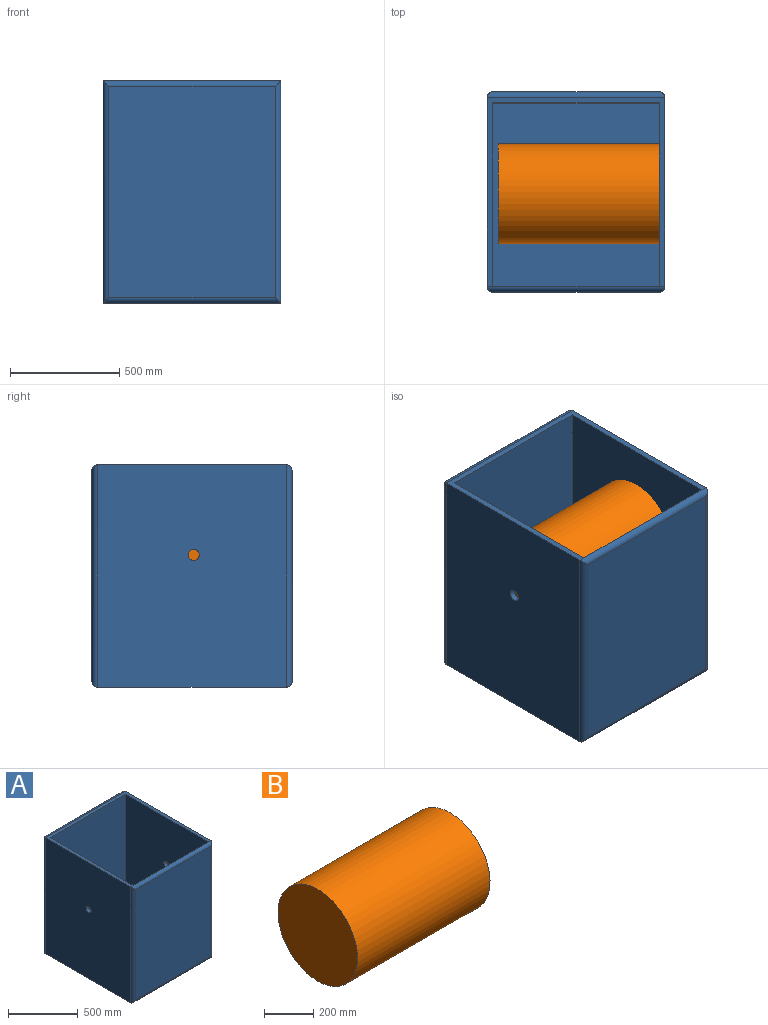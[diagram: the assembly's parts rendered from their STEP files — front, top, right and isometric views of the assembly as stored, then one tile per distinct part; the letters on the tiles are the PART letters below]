
ASSEMBLY  parts=2 mates=1
PART A: 21 faces, bbox 812.8x914.4x1016 mm
  f0: plane 863.6x812.8mm, normal (0,0,1), area 63225.7mm2, adj f2,f4,f6,f7,f9,f12,f16
  f1: plane 965.2x762mm, normal (0,1,0), area 735482.4mm2, adj f11,f12,f13,f14
  f2: plane 1016x863.6mm, normal (-1,0,0), area 875390.8mm2, adj f0,f5,f14,f18,f20
  f3: plane 965.2x762mm, normal (0,-1,0), area 735482.4mm2, adj f15,f16,f17,f18
  f4: plane 1016x863.6mm, normal (1,0,0), area 875390.8mm2, adj f0,f5,f11,f15,f19
  f5: plane 863.6x812.8mm, normal (0,0,-1), area 701934.1mm2, adj f2,f4,f13,f17
  f6: plane 939.8x762mm, normal (0,-1,0), area 716127.6mm2, adj f0,f7,f9,f10
  f7: plane 939.8x838.2mm, normal (1,0,0), area 785713.5mm2, adj f0,f6,f8,f10,f20
  f8: plane 939.8x762mm, normal (0,1,0), area 716127.6mm2, adj f7,f9,f10,f16
  f9: plane 939.8x838.2mm, normal (-1,0,0), area 785713.5mm2, adj f0,f6,f8,f10,f19
  f10: plane 838.2x762mm, normal (0,0,1), area 638708.4mm2, adj f6,f7,f8,f9
  f11: cylinder r=25.4mm len=1016mm, axis (0,0,-1), area 39800.1mm2, adj f1,f4,f12,f13
  f12: cylinder r=25.4mm len=812.8mm, axis (1,0,0), area 31692.8mm2, adj f0,f1,f11,f14
  f13: cylinder r=25.4mm len=812.8mm, axis (-1,0,0), area 31692.8mm2, adj f1,f5,f11,f14
  f14: cylinder r=25.4mm len=1016mm, axis (0,0,1), area 39800.1mm2, adj f1,f2,f12,f13
  f15: cylinder r=25.4mm len=1016mm, axis (0,0,1), area 39800.1mm2, adj f3,f4,f16,f17
  f16: cylinder r=25.4mm len=812.8mm, axis (-1,0,0), area 31692.8mm2, adj f0,f3,f8,f15,f18
  f17: cylinder r=25.4mm len=812.8mm, axis (1,0,0), area 31692.8mm2, adj f3,f5,f15,f18
  f18: cylinder r=25.4mm len=1016mm, axis (0,0,-1), area 39800.1mm2, adj f2,f3,f16,f17
  f19: cylinder r=25.4mm len=50.8mm, axis (1,0,0), area 4053.7mm2, adj f4,f9
  f20: cylinder r=25.4mm len=50.8mm, axis (1,0,0), area 4053.7mm2, adj f2,f7
PART B: 3 faces, bbox 762x457.2x457.2 mm
  f0: cylinder r=228.6mm len=762mm, axis (-1,0,0), area 1094488.2mm2, adj f1,f2
  f1: plane 457.2x457.2mm, normal (1,0,0), area 164173.2mm2, adj f0
  f2: plane 457.2x457.2mm, normal (-1,0,0), area 164173.2mm2, adj f0
PLACE A t=(-603.51,54.22,-454.51)mm
PLACE B rot(axis=(-1,0,0),5.3deg) t=(-1067.41,54.22,150.17)mm
MATE revolute B.f0 <-> A.f19  axis (1,0,0) through (-305.41,54.22,150.17)mm
